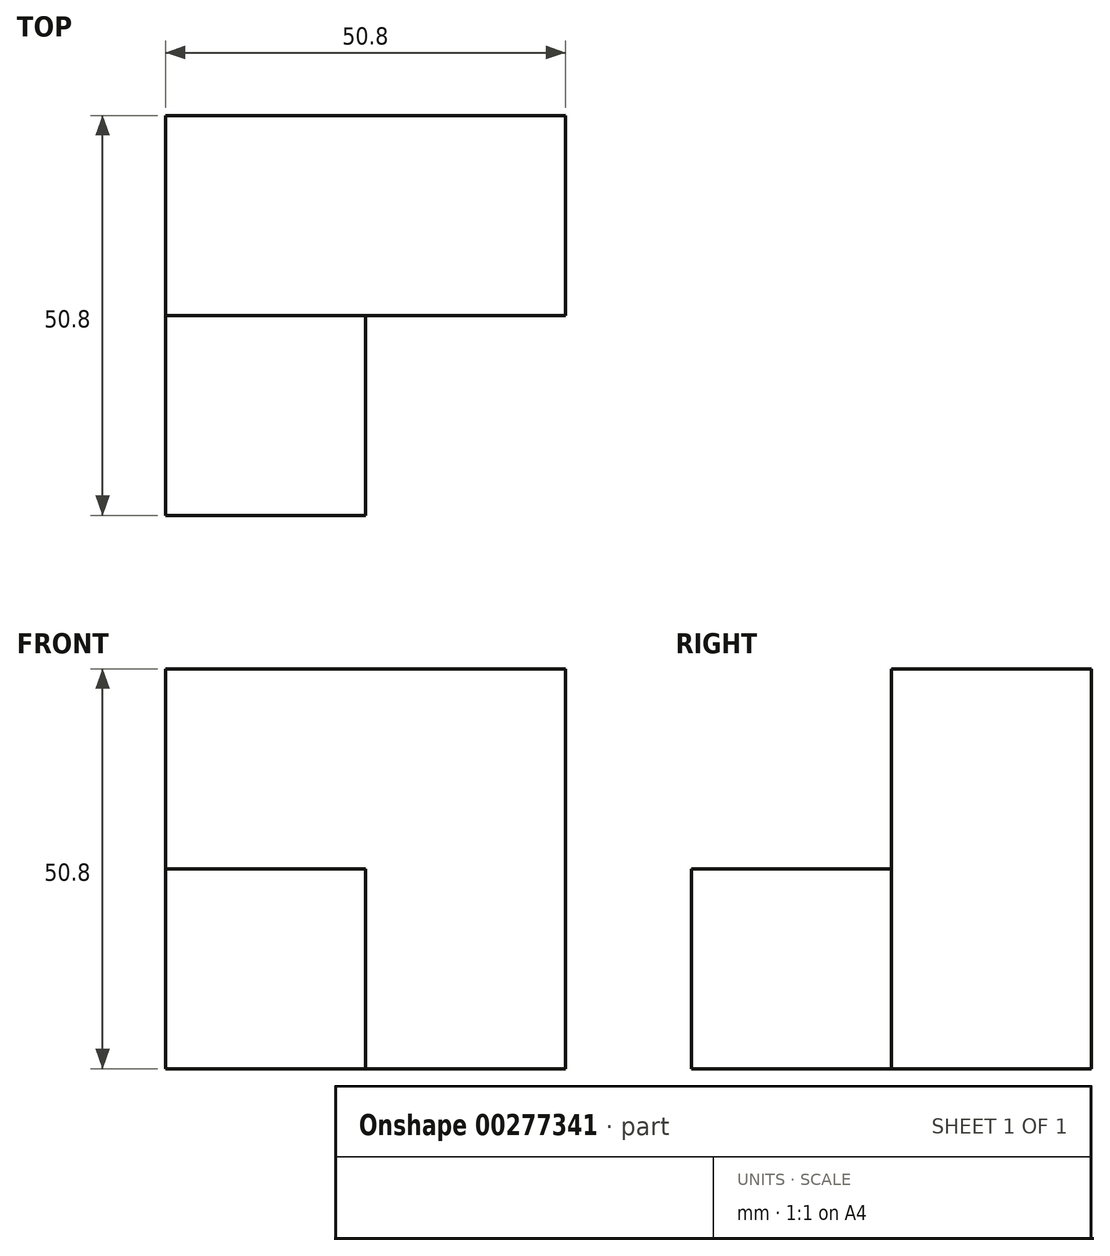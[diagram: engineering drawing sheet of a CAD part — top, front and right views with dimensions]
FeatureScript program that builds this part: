
annotation { "Feature Type Name" : "Feature", "Feature Type Description" : "" }
export const myFeature = defineFeature(function(context is Context, id is Id, definition is map)
    precondition{}
    {
        {
            var Q0;
            Q0=qCreatedBy(makeId("Front.planeOp"),FACE);
            var sketch = newSketch(context, id + "F0", { "sketchPlane" : qUnion([Q0])});
            skLineSegment(sketch, "E0.bottom", {"start": v(-53.4, -45.15) * mm, "end": v(-28, -45.15) * mm});
            skLineSegment(sketch, "E0.top", {"start": v(-53.4, -70.55) * mm, "end": v(-28, -70.55) * mm});
            skLineSegment(sketch, "E0.left", {"start": v(-53.4, -45.15) * mm, "end": v(-53.4, -70.55) * mm});
            skLineSegment(sketch, "E0.right", {"start": v(-28, -45.15) * mm, "end": v(-28, -70.55) * mm});
            skSolve(sketch);
        }
        {
            var Q0;
            Q0 = qSketchRegion(id + "F0", true);
            extrude(context, id + "F1", {"entities" : qUnion([Q0]), "depth" : 50.8 * mm});
        }
        {
            var Q0;
            Q0=makeQuery(id+"F1.opExtrude","SWEPT_FACE",FACE,{"disambiguationData":[OSD([sQuery(id+"F0.wireOp",EDGE,"E0.bottom")])]});
            var sketch = newSketch(context, id + "F2", { "sketchPlane" : qUnion([Q0])});
            skLineSegment(sketch, "E1.bottom", {"start": v(-53.4, 0) * mm, "end": v(-28, 0) * mm});
            skLineSegment(sketch, "E1.top", {"start": v(-53.4, -25.4) * mm, "end": v(-28, -25.4) * mm});
            skLineSegment(sketch, "E1.left", {"start": v(-53.4, 0) * mm, "end": v(-53.4, -25.4) * mm});
            skLineSegment(sketch, "E1.right", {"start": v(-28, 0) * mm, "end": v(-28, -25.4) * mm});
            skSolve(sketch);
        }
        {
            var Q0;
            Q0 = qSketchRegion(id + "F2", true);
            extrude(context, id + "F3", {"entities" : qUnion([Q0]), "operationType" : NewBodyOperationType.ADD, "depth" : 25.4 * mm});
        }
        {
            var Q0;
            Q0=makeQuery(id+"F3.boolean.opBoolean","MERGE",FACE,{"derivedFrom":[makeQuery(id+"F1.opExtrude","SWEPT_FACE",FACE,{"disambiguationData":[OSD([sQuery(id+"F0.wireOp",EDGE,"E0.right")])]}),makeQuery(id+"F3.opExtrude","SWEPT_FACE",FACE,{"disambiguationData":[OSD([sQuery(id+"F2.wireOp",EDGE,"E1.right")])]})]});
            var sketch = newSketch(context, id + "F4", { "sketchPlane" : qUnion([Q0])});
            skLineSegment(sketch, "E2.bottom", {"start": v(-25.4, -19.75) * mm, "end": v(0, -19.75) * mm});
            skLineSegment(sketch, "E2.top", {"start": v(-25.4, -70.55) * mm, "end": v(0, -70.55) * mm});
            skLineSegment(sketch, "E2.left", {"start": v(-25.4, -19.75) * mm, "end": v(-25.4, -70.55) * mm});
            skLineSegment(sketch, "E2.right", {"start": v(0, -19.75) * mm, "end": v(0, -70.55) * mm});
            skSolve(sketch);
        }
        {
            var Q0;
            Q0 = qSketchRegion(id + "F4", true);
            extrude(context, id + "F5", {"entities" : qUnion([Q0]), "operationType" : NewBodyOperationType.ADD, "depth" : 25.4 * mm});
        }
    });
